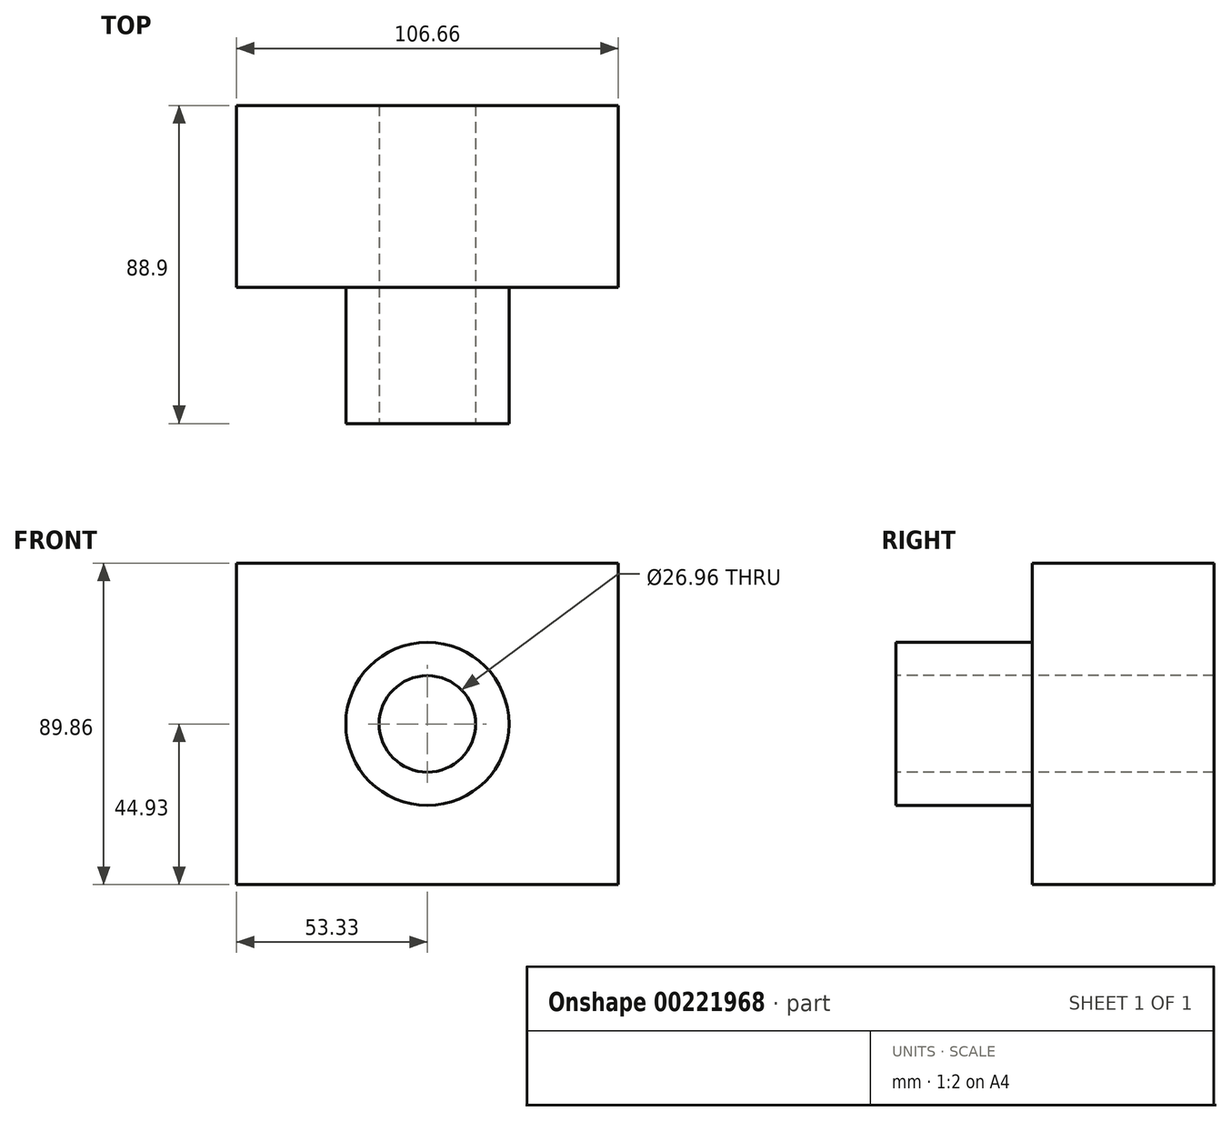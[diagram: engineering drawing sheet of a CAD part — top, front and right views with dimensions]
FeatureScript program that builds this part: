
annotation { "Feature Type Name" : "Feature", "Feature Type Description" : "" }
export const myFeature = defineFeature(function(context is Context, id is Id, definition is map)
    precondition{}
    {
        {
            var Q0;
            Q0=qCreatedBy(makeId("Front.planeOp"),FACE);
            var sketch = newSketch(context, id + "F0", { "sketchPlane" : qUnion([Q0])});
            skCircle(sketch, "E0", {"center": v(0, 0) * mm, "radius": 13.48 * mm});
            skCircle(sketch, "E1", {"center": v(0, 0) * mm, "radius": 22.8 * mm});
            skLineSegment(sketch, "E2", {"start": v(0, 44.93) * mm, "end": v(-53.33, 44.93) * mm});
            skLineSegment(sketch, "E3", {"start": v(-53.33, 44.93) * mm, "end": v(-53.33, 0) * mm});
            skLineSegment(sketch, "E4.MirrorCS", {"start": v(0, -44.93) * mm, "end": v(-53.33, -44.93) * mm});
            skLineSegment(sketch, "E5.MirrorCS", {"start": v(-53.33, -44.93) * mm, "end": v(-53.33, 0) * mm});
            skLineSegment(sketch, "E6.MirrorCS", {"start": v(0, -44.93) * mm, "end": v(53.33, -44.93) * mm});
            skLineSegment(sketch, "E7.MirrorCS", {"start": v(53.33, -44.93) * mm, "end": v(53.33, 0) * mm});
            skLineSegment(sketch, "E8.MirrorCS", {"start": v(53.33, 44.93) * mm, "end": v(53.33, 0) * mm});
            skLineSegment(sketch, "E9.MirrorCS", {"start": v(0, 44.93) * mm, "end": v(53.33, 44.93) * mm});
            skSolve(sketch);
        }
        {
            var Q0;
            Q0=makeQuery(id+"F0.imprint","IMPRINT",FACE,{"disambiguationData":[TD([[makeQuery(id+"F0.imprint","IMPRINT",EDGE,{"derivedFrom":sQuery(id+"F0.wireOp",EDGE,"E1")}),-1.0]])]});
            var Q1;
            Q1=makeQuery(id+"F0.imprint","IMPRINT",FACE,{"disambiguationData":[TD([[makeQuery(id+"F0.imprint","IMPRINT",EDGE,{"derivedFrom":sQuery(id+"F0.wireOp",EDGE,"E0")}),-1.0]])]});
            extrude(context, id + "F1", {"entities" : qUnion([Q0, Q1]), "oppositeDirection" : true, "depth" : 50.8 * mm});
        }
        {
            var Q0;
            Q0=makeQuery(id+"F0.imprint","IMPRINT",FACE,{"disambiguationData":[TD([[makeQuery(id+"F0.imprint","IMPRINT",EDGE,{"derivedFrom":sQuery(id+"F0.wireOp",EDGE,"E0")}),-1.0]])]});
            extrude(context, id + "F2", {"entities" : qUnion([Q0]), "operationType" : NewBodyOperationType.ADD, "depth" : 38.1 * mm});
        }
    });
